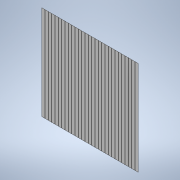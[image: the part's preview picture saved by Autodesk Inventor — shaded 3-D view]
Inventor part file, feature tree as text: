
AUTODESK INVENTOR PART (.ipt)
format: ipt  version: 2021 (Build 250183000, 183)  size: 215,552 bytes
history: native  units: in
note: dims shown in document units (in); Inventor stores cm internally (conversion verified against a paired STEP export)
features: extrude x3, sketch x3, pattern_linear x1, projected_geometry x1
ambient origin geometry x8: Origin, YZ Plane, XZ Plane, XY Plane, X Axis, Y Axis, Z Axis, Center Point
bodies: Solid1 (feature_tree)
feature tree (8):
  extrude  "Extrusion1"  Depth=3.0in
  extrude  "Extrusion2"  Depth=0.1in
  pattern_linear  "Rectangular Pattern1"  Count1=29 Spacing1=0.106in
  extrude  "Extrusion3"  Depth=0.106in TaperAngle=0.0deg
  sketch  "Sketch1"  dims[d0=4.0in d1=3.0in]
  sketch  "Sketch2"  dims[d2=0.04in d3=0.0in d4=0.1in]
  projected_geometry  "Projected Loop1"
  sketch  "Sketch3"  dims[d5=0.0015in d6=0.0in d7=11.4173in d9=0.106in d10=1.0in d11=0.0in]
